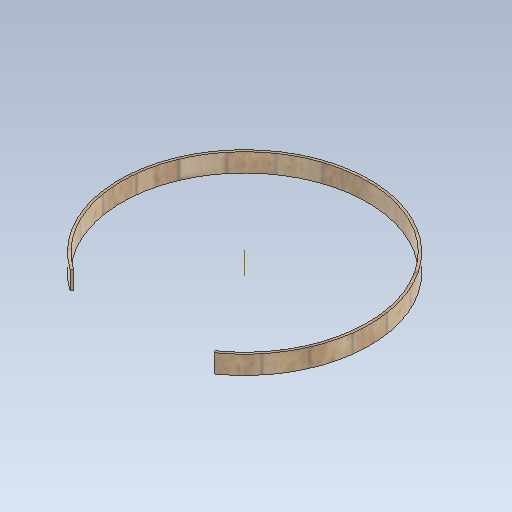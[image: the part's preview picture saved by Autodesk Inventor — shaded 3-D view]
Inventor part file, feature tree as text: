
AUTODESK INVENTOR PART (.ipt)
format: ipt  version: 2020 (Build 240168000, 168)  size: 138,752 bytes
history: native  units: mm
features: extrude x1
ambient origin geometry x8: Origin, YZ Plane, XZ Plane, XY Plane, X Axis, Y Axis, Z Axis, Center Point
bodies: Solid1 (feature_tree)
feature tree (1):
  extrude  "Extrusion1"  Depth=400.0mm
